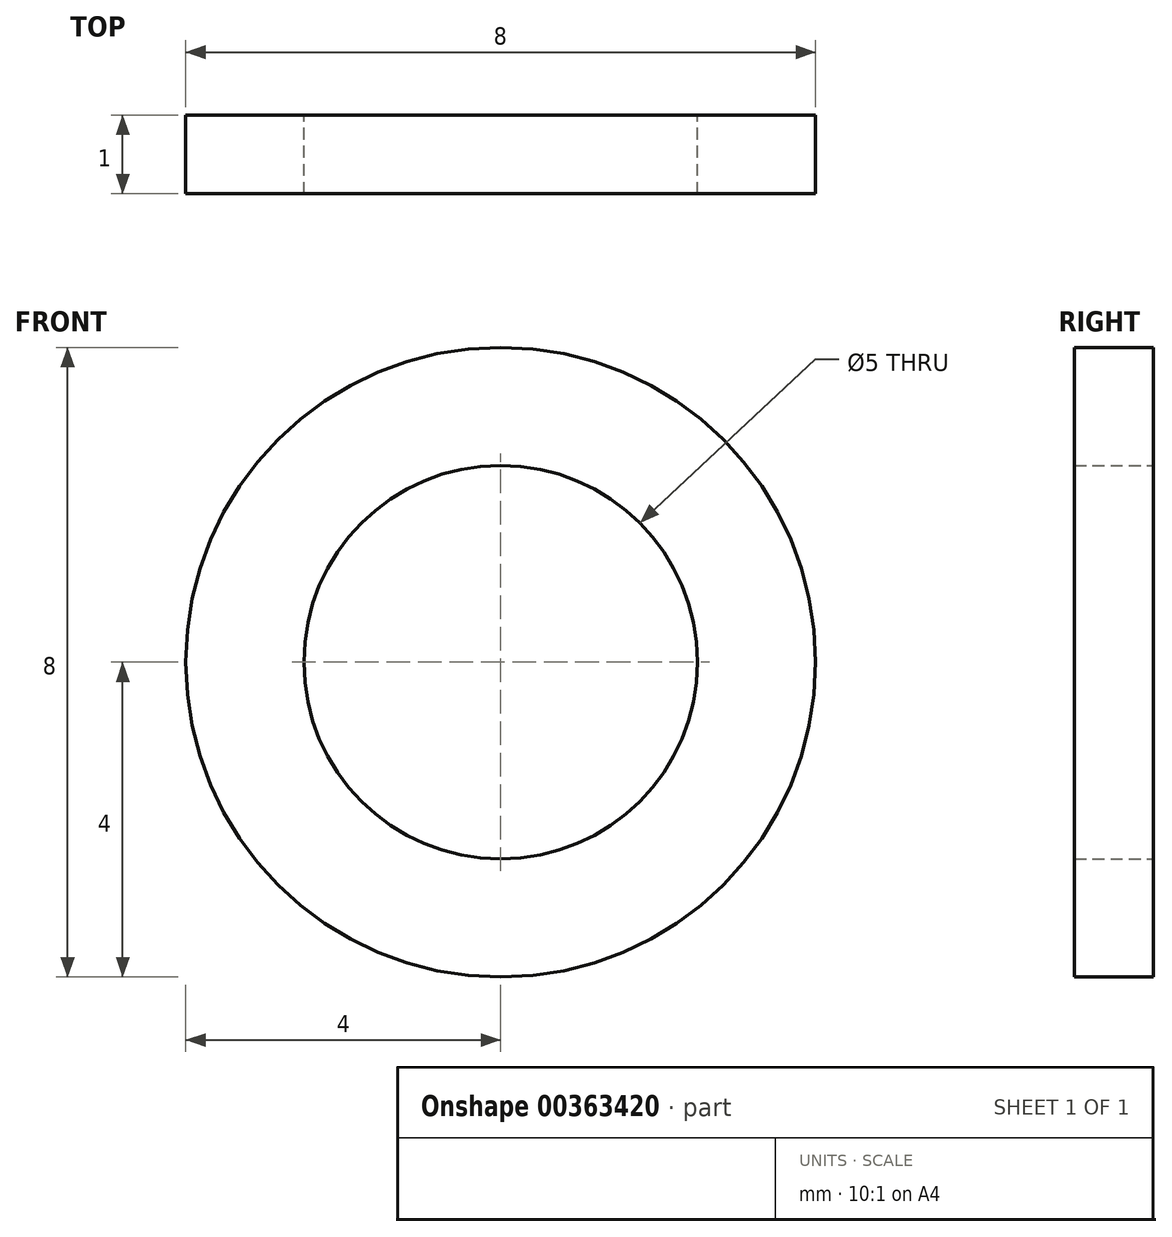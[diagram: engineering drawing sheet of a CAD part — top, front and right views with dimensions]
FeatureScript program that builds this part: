
annotation { "Feature Type Name" : "Feature", "Feature Type Description" : "" }
export const myFeature = defineFeature(function(context is Context, id is Id, definition is map)
    precondition{}
    {
        {
            var Q0;
            Q0=qCreatedBy(makeId("Front.planeOp"),FACE);
            var sketch = newSketch(context, id + "F0", { "sketchPlane" : qUnion([Q0])});
            skCircle(sketch, "E0", {"center": v(0, 0) * mm, "radius": 2.5 * mm});
            skCircle(sketch, "E1", {"center": v(0, 0) * mm, "radius": 4 * mm});
            skSolve(sketch);
        }
        {
            var Q0;
            Q0=makeQuery(id+"F0.imprint","IMPRINT",FACE,{"disambiguationData":[TD([[makeQuery(id+"F0.imprint","IMPRINT",EDGE,{"derivedFrom":sQuery(id+"F0.wireOp",EDGE,"E0")}),-1.0]])]});
            extrude(context, id + "F1", {"entities" : qUnion([Q0]), "depth" : 1 * mm, "offsetDistance" : 25 * mm});
        }
    });
